# Revit family: P500285-015
name_source: partatom
category: Lighting Fixtures
revit_build: Autodesk Revit 2014 (Build: 20130308_1515(x64)
units: mm (PartAtom-declared; Revit-internal decimal feet)

## types (1)
- P500285-015
    Apparent Load = 40 VA
    Assembly Code = D5020200
    Connector Description = Lighting Connector
    Default Elevation = 48 "
    Description = Inspired at its roots by an understated beauty and a breathtaking formal elegance, the Bonita Collection Four-Light Polished Chrome Foyer Chandelier will make a stunning addition to any luxurious living space. A magnificent silver cage embraces the drum shades in a teardrop fashion with four chrome arms flowing down from an ornamental circular plate near the top of the design. The shades are held in place by silver candlestick light bases supported by elegantly curved arms.
    Features = Magnificent polished chrome cage embraces the drum shades in teardrop fashion.
Four polished chrome arms flow down from an ornamental circular plate near the top of the design.
Polished chrome candlestick light bases supported by elegantly curved arms hold the drum shades in place.
Ideal for any foyer, entryway, or kitchen.
Elegant choice for modern, luxury, or transitional interiors.
Measures 23-inches width by 25-7/8-inch height.
Uses four candelabra base bulbs that are sold separately (40w max - LED or incandescent).
Able to be fully dimmable with dimmable bulbs.
Includes installation instructions and mounting hardware.
Progress Lighting products are designed for exceptional quality, reliability, and functionality.
    Fixture distribution = Direct
    Glass = Paint - Hubbell - White Texture
    Gold = Hubbell - Gold
    Height = 11 "
    Housing Material = Paint - Hubbell - Light Silver
    Lamp = LED or Medium Base
    Load Classification = Lighting
    Manufacturer = Progress Lighting
    Model = P500285-015
    Power Factor = 1
    Product Documentation Link = https://hubbellcdn.com
    Product Link = https://www.hubbell.com
    Square = 6 "
    URL = https://www.hubbell.com
    Voltage = 120 V
    Warranty = 1 year Warranty
    Wattage Comments = 40W
    Watts = 40 W

## geometry (parser evidence)
native form markers: Sweep x4
no freeform markers — native parametric forms only
